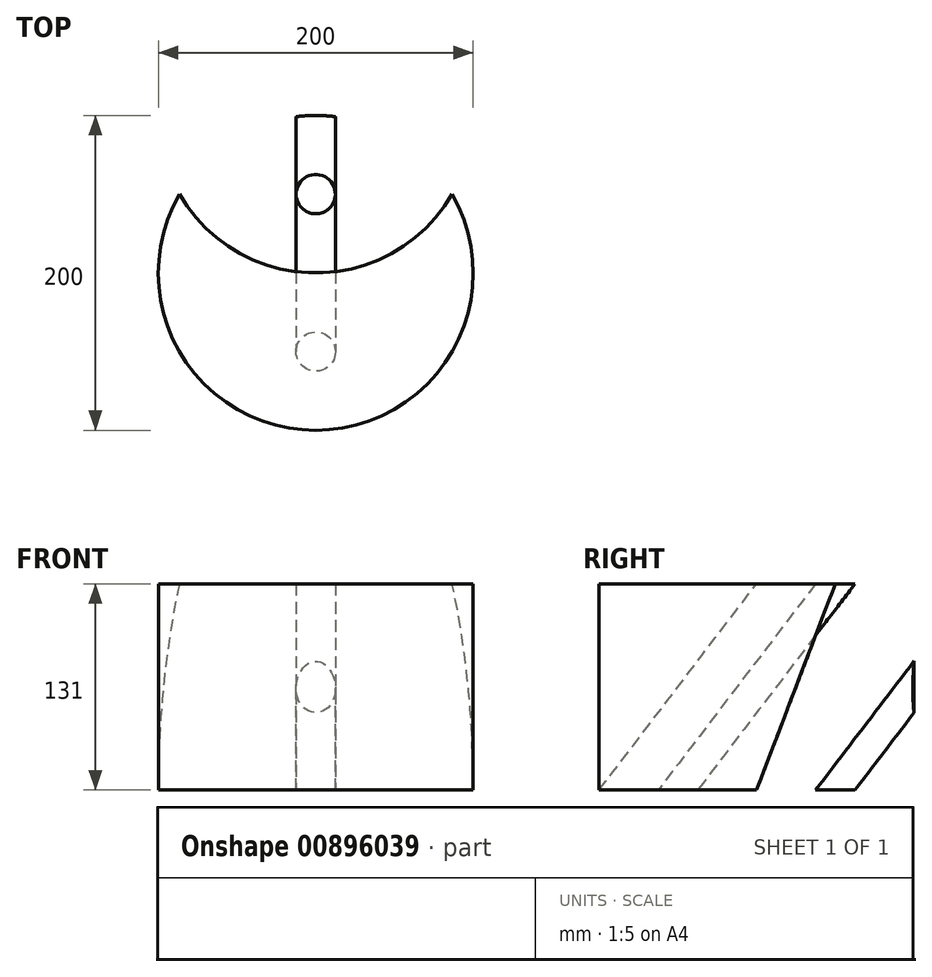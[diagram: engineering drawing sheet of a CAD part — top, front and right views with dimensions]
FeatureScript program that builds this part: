
annotation { "Feature Type Name" : "Feature", "Feature Type Description" : "" }
export const myFeature = defineFeature(function(context is Context, id is Id, definition is map)
    precondition{}
    {
        {
            var Q0;
            Q0=qCreatedBy(makeId("Top.planeOp"),FACE);
            var sketch = newSketch(context, id + "F0", { "sketchPlane" : qUnion([Q0])});
            skCircle(sketch, "E0", {"center": v(0, 0) * mm, "radius": 100 * mm});
            skSolve(sketch);
        }
        {
            var Q0;
            Q0=makeQuery(id+"F0.imprint","IMPRINT",FACE,{"disambiguationData":[TD([[makeQuery(id+"F0.imprint","IMPRINT",EDGE,{"derivedFrom":sQuery(id+"F0.wireOp",EDGE,"E0")}),1.0]])]});
            extrude(context, id + "F1", {"entities" : qUnion([Q0]), "depth" : 131 * mm, "offsetDistance" : 25 * mm});
        }
        {
            var Q0;
            Q0=makeQuery(id+"F1.opExtrude","CAP_FACE",FACE,{"disambiguationData":[OSD([sQuery(id+"F0.wireOp",EDGE,"E0")])],"isStart":false});
            var sketch = newSketch(context, id + "F2", { "sketchPlane" : qUnion([Q0])});
            skLineSegment(sketch, "E1", {"start": v(0, 0) * mm, "end": v(0, 50) * mm});
            skLineSegment(sketch, "E2", {"start": v(0, 0) * mm, "end": v(0, -50) * mm});
            skCircle(sketch, "E3", {"center": v(0, -50) * mm, "radius": 12.5 * mm});
            skCircle(sketch, "E4", {"center": v(0, 50) * mm, "radius": 12.5 * mm});
            skSolve(sketch);
        }
        {
            var Q0;
            Q0=makeQuery(id+"F1.opExtrude","CAP_FACE",FACE,{"disambiguationData":[OSD([sQuery(id+"F0.wireOp",EDGE,"E0")])],"isStart":true});
            var sketch = newSketch(context, id + "F3", { "sketchPlane" : qUnion([Q0])});
            skCircle(sketch, "E5.0", {"center": v(0, 50) * mm, "radius": 12.5 * mm});
            skCircle(sketch, "E6.0", {"center": v(0, -50) * mm, "radius": 12.5 * mm});
            skSolve(sketch);
        }
        {
            var Q0;
            Q0=qCreatedBy(makeId("Right.planeOp"),FACE);
            var sketch = newSketch(context, id + "F4", { "sketchPlane" : qUnion([Q0])});
            skPoint(sketch, "E7.0", {"position": v(-50, 0) * mm});
            skPoint(sketch, "E8.0", {"position": v(50, 131) * mm});
            skLineSegment(sketch, "E9", {"start": v(50, 131) * mm, "end": v(-50, 0) * mm});
            skSolve(sketch);
        }
        {
            var Q0;
            Q0=makeQuery(id+"F3.imprint","IMPRINT",FACE,{"disambiguationData":[TD([[makeQuery(id+"F3.imprint","IMPRINT",EDGE,{"derivedFrom":sQuery(id+"F3.wireOp",EDGE,"E5.0")}),-1.0]])]});
            var Q1;
            Q1=sQuery(id+"F4.wireOp",EDGE,"E9");
            sweep(context, id + "F5", {"operationType" : NewBodyOperationType.REMOVE, "profiles" : qUnion([Q0]), "path" : qUnion([Q1])});
        }
    });
